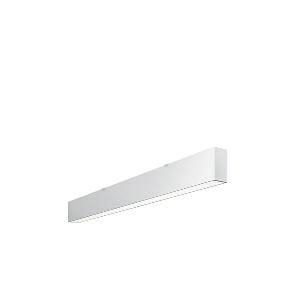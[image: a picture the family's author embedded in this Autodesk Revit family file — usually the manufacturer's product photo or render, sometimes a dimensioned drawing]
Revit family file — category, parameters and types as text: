
# Revit family: dotoo_line_-_dla_1000_840_d_end_00807927_46ed
name_source: partatom
category: Lighting Fixtures
units: mm (PartAtom-declared; Revit-internal decimal feet)

## family parameters
Cut with Voids When Loaded = No
Host = Face
Light Source = No
Part Type = Normal
Room Calculation Point = No
Round Connector Dimension = Use Diameter
Shared = No

## types (1)
- DOTOO.line - DLA 1000/840/D END (1 x LED, 1000 lm, 4000K)
    Apparent Load = 10 VA
    Approval mark = CE
    CIE Flux Codes = 67 91 98 100 100
    Color Rendering = 80-89
    Color Temperature = 4000K
    Control Gear = Electronic ballast
    Default Elevation = 1800 mm
    Description = DLA 1000/840/D|Surface-mounted luminaire.|light source: LED|work equipment: Adjustable electronic ballast, digital DALI|connected load: 220-240 V, 50/60 Hz|Power consumption: approx. 9,5 W|luminous flux: 1000 lm|luminous efficacy: 105 lm/W|light distribution: Direct|colour temperature: Cold white, ca. 4000 K|class of protection: I|technology: Continuously dimmable|mains lead: Connector|glare control: Prism aperture|special features: DALI Load 1x, TouchDIM - dimming via standard switch, Through-wired, up to 18 m on one mains connection, Flicker-free, Suitable as emergency lighting, Mechanical and electrical connection of the individual modules without tools|
    Frequency = 50 Hz
    Height = 110 mm
    Lamp = 1 x LED
    Lamp Light Flux = 1000 lm
    Lamp count = 1
    Length = 848 mm
    Luminous efficacy = 105 lm/W
    Manufacturer = Waldmann
    ModVariant = No
    Model = 00807927
    Mounting Place = Ceiling
    Mounting Type = Surface mounted
    Number of Poles = 1
    OnlyDefault = Yes
    Power Factor = 1
    Product Name = DOTOO.line - DLA 1000/840/D END
    Product group = Ceiling mounted luminaire
    ProductGroupID = 3
    Protection Class = Protection class I
    Protection Degree = IP 40
    RLX_Detail_Level = 1
    RLX_Emergency_Light_Flux = 0 lm
    RLX_Emergency_Type = 0
    RLX_Emergency_Type_DB = No
    RlxData = <blob elided: 15237 chars, md5=aff4388a>
    Socket = socket
    Standby Power = 0 W
    System Light Flux = 1000 lm
    System Power = 10 W
    Type Comments = Product without accessories
    Type Image = 114350000-00807927.jpg
    URL = http://relux.com
    VarID = ---
    Voltage = 230 V
    Voltage Range = 220-240 V
    Weight = 0.00 kg
    Width = 60 mm  [stored 0.19685 ft]

note: [stored X ft] marks values corroborated as IEEE doubles in the binary element streams (Revit-internal decimal feet)

## geometry (parser evidence)
native form markers: Sweep x11
no freeform markers — native parametric forms only
